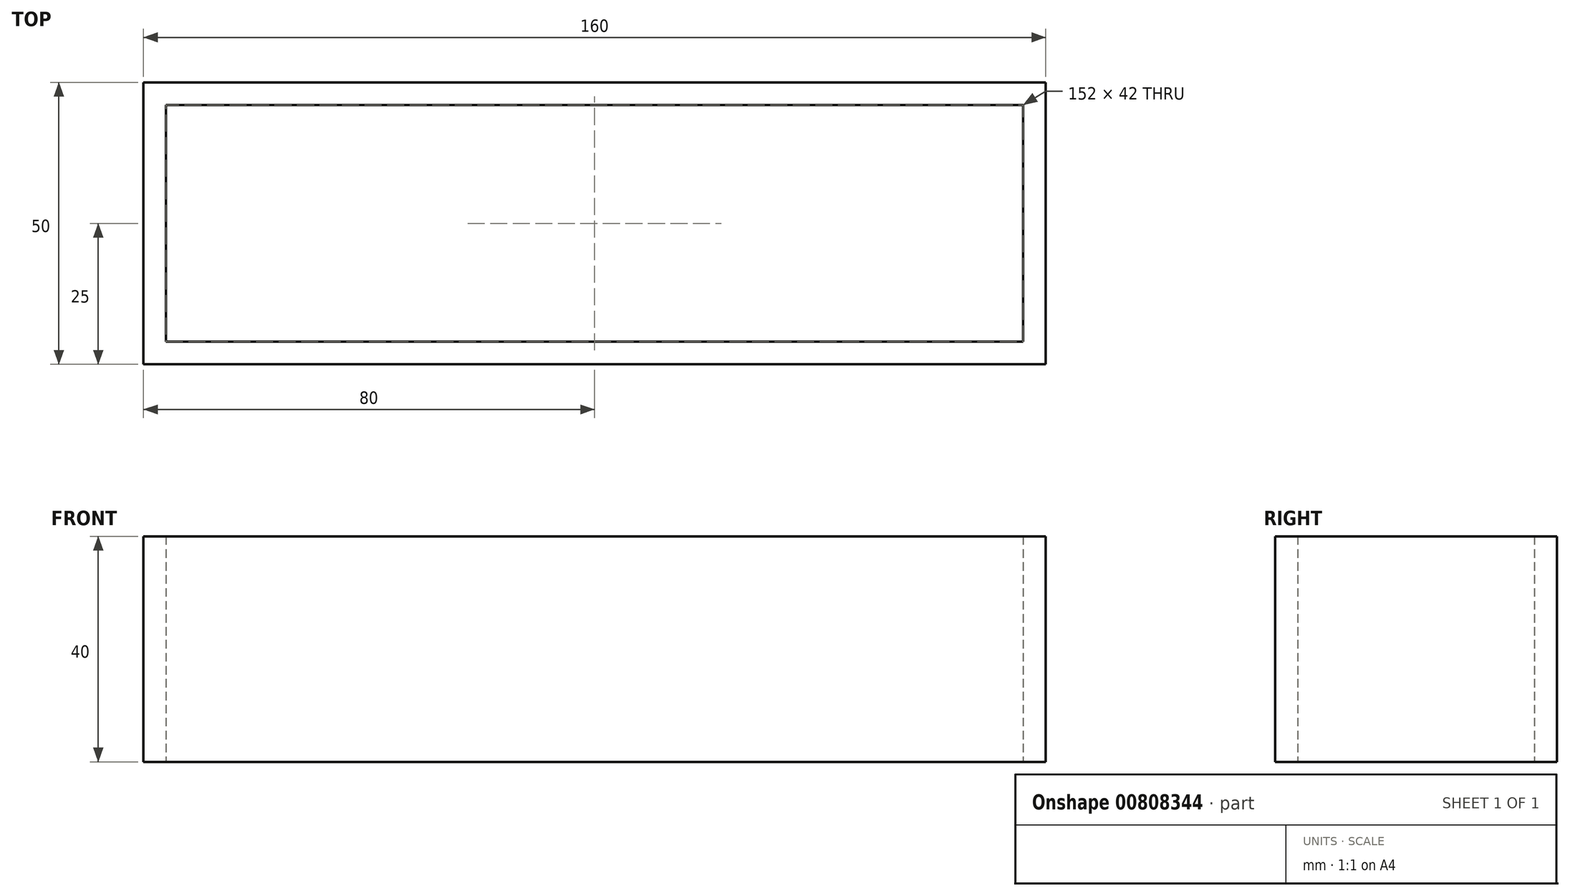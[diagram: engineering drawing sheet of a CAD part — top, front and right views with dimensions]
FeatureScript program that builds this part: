
annotation { "Feature Type Name" : "Feature", "Feature Type Description" : "" }
export const myFeature = defineFeature(function(context is Context, id is Id, definition is map)
    precondition{}
    {
        {
            var Q0;
            Q0=qCreatedBy(makeId("Top.planeOp"),FACE);
            var sketch = newSketch(context, id + "F0", { "sketchPlane" : qUnion([Q0])});
            skLineSegment(sketch, "E0.bottom", {"start": v(0, 0) * mm, "end": v(160, 0) * mm});
            skLineSegment(sketch, "E0.top", {"start": v(0, 50) * mm, "end": v(160, 50) * mm});
            skLineSegment(sketch, "E0.left", {"start": v(0, 0) * mm, "end": v(0, 50) * mm});
            skLineSegment(sketch, "E0.right", {"start": v(160, 0) * mm, "end": v(160, 50) * mm});
            skLineSegment(sketch, "E1.0", {"start": v(4, 46) * mm, "end": v(156, 46) * mm});
            skLineSegment(sketch, "E1.1", {"start": v(4, 4) * mm, "end": v(4, 46) * mm});
            skLineSegment(sketch, "E1.2", {"start": v(4, 4) * mm, "end": v(156, 4) * mm});
            skLineSegment(sketch, "E1.3", {"start": v(156, 4) * mm, "end": v(156, 46) * mm});
            skSolve(sketch);
        }
        {
            var Q0;
            Q0=makeQuery(id+"F0.imprint","IMPRINT",FACE,{"disambiguationData":[TD([[makeQuery(id+"F0.imprint","IMPRINT",EDGE,{"derivedFrom":sQuery(id+"F0.wireOp",EDGE,"E0.bottom")}),1.0]])]});
            extrude(context, id + "F1", {"entities" : qUnion([Q0]), "depth" : 40 * mm, "offsetDistance" : 25 * mm});
        }
    });
